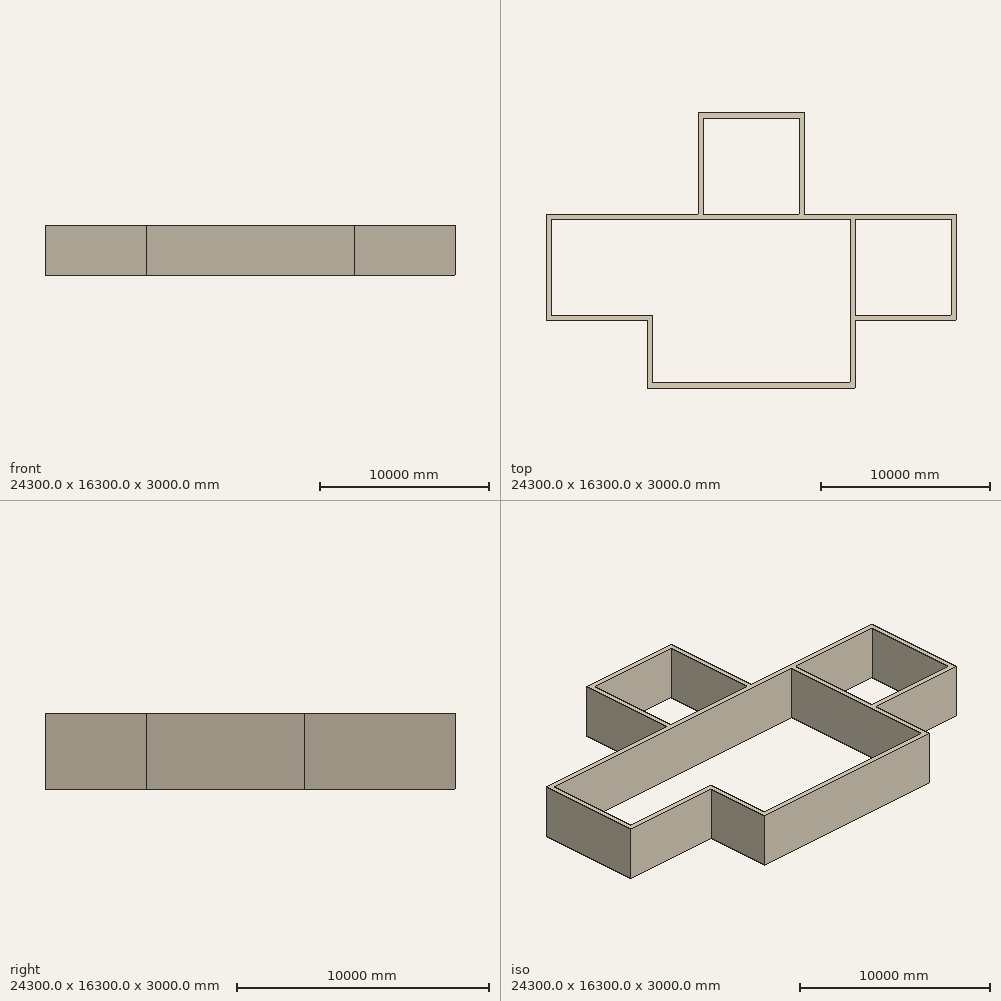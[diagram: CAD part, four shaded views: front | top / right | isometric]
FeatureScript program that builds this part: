
annotation { "Feature Type Name" : "Feature", "Feature Type Description" : "" }
export const myFeature = defineFeature(function(context is Context, id is Id, definition is map)
    precondition{}
    {
        {
            var Q0;
            Q0=qCreatedBy(makeId("Top.planeOp"),FACE);
            var sketch = newSketch(context, id + "F0", { "sketchPlane" : qUnion([Q0])});
            skLineSegment(sketch, "E0.bottom", {"start": v(-5296.05, 0) * mm, "end": v(6703.95, 0) * mm});
            skLineSegment(sketch, "E0.top", {"start": v(-5296.05, -10000) * mm, "end": v(6703.95, -10000) * mm});
            skLineSegment(sketch, "E0.left", {"start": v(-5296.05, -6000) * mm, "end": v(-5296.05, -10000) * mm});
            skLineSegment(sketch, "E0.right", {"start": v(6703.95, 0) * mm, "end": v(6703.95, -10000) * mm});
            skLineSegment(sketch, "E1.bottom", {"start": v(6703.95, 0) * mm, "end": v(12703.95, 0) * mm});
            skLineSegment(sketch, "E1.top", {"start": v(6703.95, -6000) * mm, "end": v(12703.95, -6000) * mm});
            skLineSegment(sketch, "E1.left", {"start": v(6703.95, 0) * mm, "end": v(6703.95, -6000) * mm});
            skLineSegment(sketch, "E1.right", {"start": v(12703.95, 0) * mm, "end": v(12703.95, -6000) * mm});
            skLineSegment(sketch, "E2.bottom", {"start": v(-2296.05, 0) * mm, "end": v(3703.95, 0) * mm});
            skLineSegment(sketch, "E2.top", {"start": v(-2296.05, 6000) * mm, "end": v(3703.95, 6000) * mm});
            skLineSegment(sketch, "E2.left", {"start": v(-2296.05, 0) * mm, "end": v(-2296.05, 6000) * mm});
            skLineSegment(sketch, "E2.right", {"start": v(3703.95, 0) * mm, "end": v(3703.95, 6000) * mm});
            skLineSegment(sketch, "E3.bottom", {"start": v(-5296.05, 0) * mm, "end": v(-11296.05, 0) * mm});
            skLineSegment(sketch, "E3.top", {"start": v(-5296.05, -6000) * mm, "end": v(-11296.05, -6000) * mm});
            skLineSegment(sketch, "E3.right", {"start": v(-11296.05, 0) * mm, "end": v(-11296.05, -6000) * mm});
            skSolve(sketch);
        }
        {
            var Q0;
            Q0=makeQuery(id+"F0.imprint","IMPRINT",FACE,{"disambiguationData":[TD([[makeQuery(id+"F0.imprint","IMPRINT",EDGE,{"derivedFrom":sQuery(id+"F0.wireOp",EDGE,"E0.top")}),1.0]])]});
            var sketch = newSketch(context, id + "F1", { "sketchPlane" : qUnion([Q0])});
            skLineSegment(sketch, "E4.0", {"start": v(-5146.05, -9850) * mm, "end": v(6553.95, -9850) * mm});
            skLineSegment(sketch, "E4.1", {"start": v(-5146.05, -5850) * mm, "end": v(-5146.05, -9850) * mm});
            skLineSegment(sketch, "E4.2", {"start": v(6553.95, -9850) * mm, "end": v(6553.95, -6000) * mm});
            skLineSegment(sketch, "E4.3", {"start": v(-11146.05, -5850) * mm, "end": v(-5146.05, -5850) * mm});
            skLineSegment(sketch, "E4.4", {"start": v(-11146.05, -150) * mm, "end": v(-11146.05, -5850) * mm});
            skLineSegment(sketch, "E4.5", {"start": v(-5296.05, -150) * mm, "end": v(-11146.05, -150) * mm});
            skLineSegment(sketch, "E4.6", {"start": v(6553.95, -6000) * mm, "end": v(6553.95, -150) * mm});
            skLineSegment(sketch, "E4.7", {"start": v(6553.95, -150) * mm, "end": v(3703.95, -150) * mm});
            skLineSegment(sketch, "E4.8", {"start": v(3703.95, -150) * mm, "end": v(-2296.05, -150) * mm});
            skLineSegment(sketch, "E4.9", {"start": v(-2296.05, -150) * mm, "end": v(-5296.05, -150) * mm});
            skLineSegment(sketch, "E5.0", {"start": v(-5446.05, -10150) * mm, "end": v(6853.95, -10150) * mm});
            skLineSegment(sketch, "E5.1", {"start": v(-5446.05, -6150) * mm, "end": v(-5446.05, -10150) * mm});
            skLineSegment(sketch, "E5.2", {"start": v(6853.95, -10150) * mm, "end": v(6853.95, -6000) * mm});
            skLineSegment(sketch, "E5.3", {"start": v(-11446.05, -6150) * mm, "end": v(-5446.05, -6150) * mm});
            skLineSegment(sketch, "E5.4", {"start": v(-11446.05, 150) * mm, "end": v(-11446.05, -6150) * mm});
            skLineSegment(sketch, "E5.5", {"start": v(-5296.05, 150) * mm, "end": v(-11446.05, 150) * mm});
            skLineSegment(sketch, "E5.6", {"start": v(6853.95, -6000) * mm, "end": v(6853.95, 150) * mm});
            skLineSegment(sketch, "E5.7", {"start": v(6853.95, 150) * mm, "end": v(3703.95, 150) * mm});
            skLineSegment(sketch, "E5.8", {"start": v(3703.95, 150) * mm, "end": v(-2296.05, 150) * mm});
            skLineSegment(sketch, "E5.9", {"start": v(-2296.05, 150) * mm, "end": v(-5296.05, 150) * mm});
            skLineSegment(sketch, "E6.0", {"start": v(12553.95, -150) * mm, "end": v(6853.95, -150) * mm});
            skLineSegment(sketch, "E6.1", {"start": v(12553.95, -5850) * mm, "end": v(12553.95, -150) * mm});
            skLineSegment(sketch, "E6.2", {"start": v(6853.95, -5850) * mm, "end": v(12553.95, -5850) * mm});
            skLineSegment(sketch, "E6.3", {"start": v(6853.95, -150) * mm, "end": v(6853.95, -5850) * mm});
            skLineSegment(sketch, "E7.0", {"start": v(12853.95, 150) * mm, "end": v(6553.95, 150) * mm});
            skLineSegment(sketch, "E7.1", {"start": v(12853.95, -6150) * mm, "end": v(12853.95, 150) * mm});
            skLineSegment(sketch, "E7.2", {"start": v(6553.95, -6150) * mm, "end": v(12853.95, -6150) * mm});
            skLineSegment(sketch, "E7.3", {"start": v(6553.95, 150) * mm, "end": v(6553.95, -6150) * mm});
            skLineSegment(sketch, "E8.0", {"start": v(-2446.05, -150) * mm, "end": v(3853.95, -150) * mm});
            skLineSegment(sketch, "E8.1", {"start": v(-2446.05, 6150) * mm, "end": v(-2446.05, -150) * mm});
            skLineSegment(sketch, "E8.2", {"start": v(3853.95, 6150) * mm, "end": v(-2446.05, 6150) * mm});
            skLineSegment(sketch, "E8.3", {"start": v(3853.95, -150) * mm, "end": v(3853.95, 6150) * mm});
            skLineSegment(sketch, "E9.0", {"start": v(-2146.05, 150) * mm, "end": v(3553.95, 150) * mm});
            skLineSegment(sketch, "E9.1", {"start": v(-2146.05, 5850) * mm, "end": v(-2146.05, 150) * mm});
            skLineSegment(sketch, "E9.2", {"start": v(3553.95, 5850) * mm, "end": v(-2146.05, 5850) * mm});
            skLineSegment(sketch, "E9.3", {"start": v(3553.95, 150) * mm, "end": v(3553.95, 5850) * mm});
            skSolve(sketch);
        }
        {
            var Q0;
            Q0 = qSketchRegion(id + "F1", true);
            extrude(context, id + "F2", {"entities" : qUnion([Q0]), "depth" : 3000 * mm, "offsetDistance" : 25 * mm});
        }
    });
